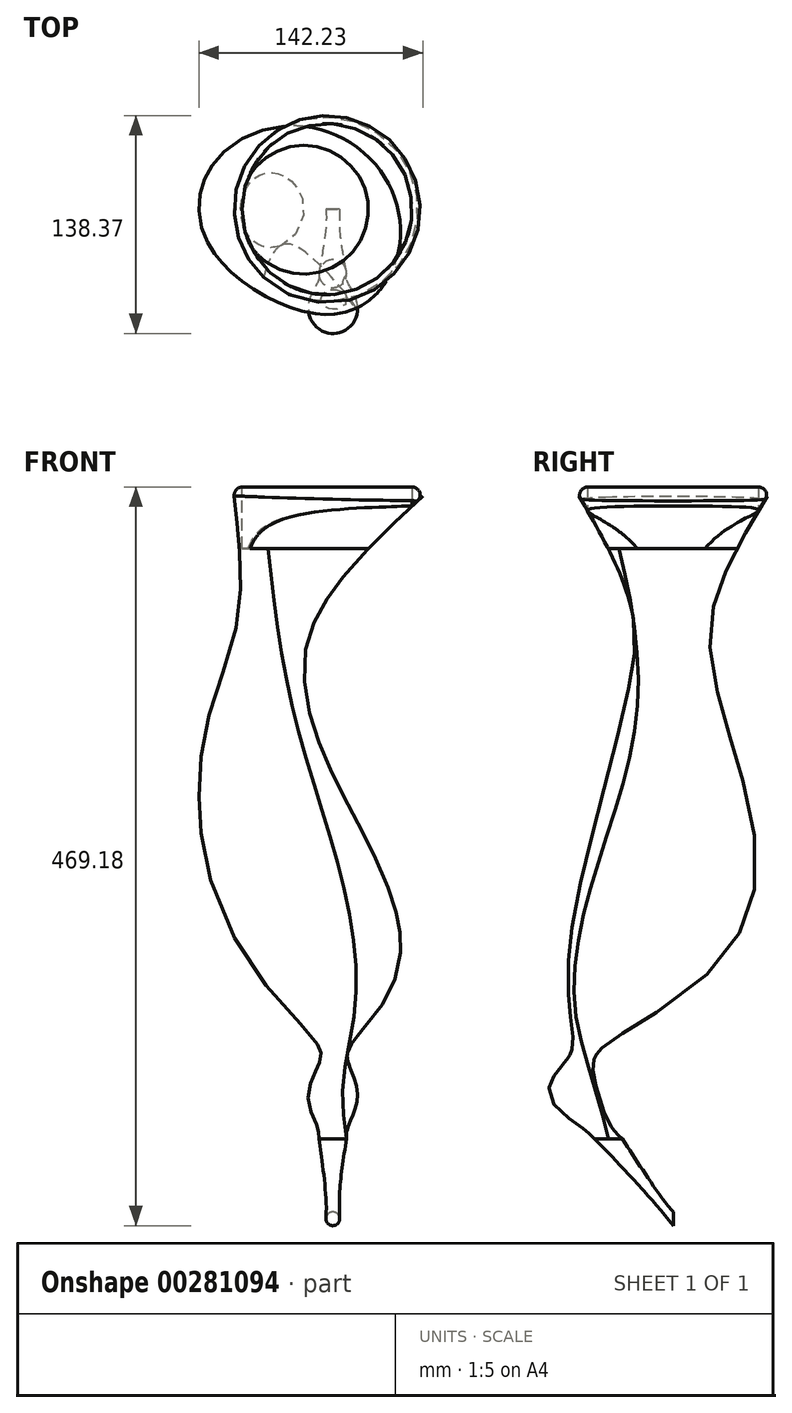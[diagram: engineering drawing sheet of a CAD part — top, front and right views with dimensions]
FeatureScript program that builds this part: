
annotation { "Feature Type Name" : "Feature", "Feature Type Description" : "" }
export const myFeature = defineFeature(function(context is Context, id is Id, definition is map)
    precondition{}
    {
        {
            var Q0;
            Q0=qCreatedBy(makeId("Front.planeOp"),FACE);
            var sketch = newSketch(context, id + "F0", { "sketchPlane" : qUnion([Q0])});
            skCircle(sketch, "E0", {"center": v(0, 0) * mm, "radius": 4.36 * mm});
            skSolve(sketch);
        }
        {
            var Q0;
            Q0=qCreatedBy(makeId("Top.planeOp"),FACE);
            cPlane(context, id + "F1", {"entities" : qUnion([Q0]), "cplaneType" : CPlaneType.OFFSET, "offset" : 50.8 * mm, "width" : 152.4 * mm, "height" : 152.4 * mm});
        }
        {
            var Q0;
            Q0=qCreatedBy(id+"F1.planeOp",FACE);
            var sketch = newSketch(context, id + "F2", { "sketchPlane" : qUnion([Q0])});
            skLineSegment(sketch, "E1", {"start": v(0, 0) * mm, "end": v(0, -41.08) * mm, "construction": true});
            skCircle(sketch, "E2", {"center": v(0, -41.08) * mm, "radius": 8.82 * mm});
            skSolve(sketch);
        }
        {
            var Q0;
            Q0=makeQuery(id+"F2.imprint","IMPRINT",FACE,{"disambiguationData":[TD([[makeQuery(id+"F2.imprint","IMPRINT",EDGE,{"derivedFrom":sQuery(id+"F2.wireOp",EDGE,"E2")}),1.0]])]});
            var Q1;
            Q1=makeQuery(id+"F0.imprint","IMPRINT",FACE,{"disambiguationData":[TD([[makeQuery(id+"F0.imprint","IMPRINT",EDGE,{"derivedFrom":sQuery(id+"F0.wireOp",EDGE,"E0")}),1.0]])]});
            loft(context, id + "F3", {"sheetProfilesArray" : [{ "sheetProfileEntities" : qUnion([Q0]) }, { "sheetProfileEntities" : qUnion([Q1]) }]});
        }
        {
            var Q0;
            Q0=qCreatedBy(id+"F1.planeOp",FACE);
            cPlane(context, id + "F4", {"entities" : qUnion([Q0]), "cplaneType" : CPlaneType.OFFSET, "offset" : 25.4 * mm, "width" : 152.4 * mm, "height" : 152.4 * mm});
        }
        {
            var Q0;
            Q0=qCreatedBy(id+"F4.planeOp",FACE);
            var sketch = newSketch(context, id + "F5", { "sketchPlane" : qUnion([Q0])});
            skLineSegment(sketch, "E3", {"start": v(0, 0) * mm, "end": v(0, -62.26) * mm, "construction": true});
            skCircle(sketch, "E4", {"center": v(0, -62.26) * mm, "radius": 15.65 * mm});
            skSolve(sketch);
        }
        {
            var Q0;
            Q0=qCreatedBy(id+"F4.planeOp",FACE);
            cPlane(context, id + "F6", {"entities" : qUnion([Q0]), "cplaneType" : CPlaneType.OFFSET, "offset" : 56.4 * mm, "width" : 152.4 * mm, "height" : 152.4 * mm});
        }
        {
            var Q0;
            Q0=qCreatedBy(id+"F6.planeOp",FACE);
            var sketch = newSketch(context, id + "F7", { "sketchPlane" : qUnion([Q0])});
            skLineSegment(sketch, "E5", {"start": v(0, 0) * mm, "end": v(0, -36.87) * mm, "construction": true});
            skCircle(sketch, "E6", {"center": v(0, -36.87) * mm, "radius": 28.94 * mm});
            skSolve(sketch);
        }
        {
            var Q0;
            Q0=qCreatedBy(id+"F6.planeOp",FACE);
            cPlane(context, id + "F8", {"entities" : qUnion([Q0]), "cplaneType" : CPlaneType.OFFSET, "offset" : 183.9 * mm, "width" : 152.4 * mm, "height" : 152.4 * mm});
        }
        {
            var Q0;
            Q0=qCreatedBy(id+"F8.planeOp",FACE);
            var sketch = newSketch(context, id + "F9", { "sketchPlane" : qUnion([Q0])});
            skLineSegment(sketch, "E7", {"start": v(0, 0) * mm, "end": v(-46.43, 0) * mm, "construction": true});
            skCircle(sketch, "E8", {"center": v(-46.43, 0) * mm, "radius": 32.98 * mm});
            skSolve(sketch);
        }
        {
            var Q0;
            Q0=qCreatedBy(id+"F8.planeOp",FACE);
            cPlane(context, id + "F10", {"entities" : qUnion([Q0]), "cplaneType" : CPlaneType.OFFSET, "offset" : 148.34 * mm, "width" : 152.4 * mm, "height" : 152.4 * mm});
        }
        {
            var Q0;
            Q0=qCreatedBy(id+"F10.planeOp",FACE);
            var sketch = newSketch(context, id + "F11", { "sketchPlane" : qUnion([Q0])});
            skCircle(sketch, "E9", {"center": v(0, 0) * mm, "radius": 63.3 * mm});
            skSolve(sketch);
        }
        {
            var Q1;
            Q1=makeQuery(id+"F3.opLoft","CAP_FACE",FACE,{"disambiguationData":[OSD([makeQuery(id+"F2.imprint","IMPRINT",FACE,{"disambiguationData":[TD([[makeQuery(id+"F2.imprint","IMPRINT",EDGE,{"derivedFrom":sQuery(id+"F2.wireOp",EDGE,"E2")}),1.0]])]})])],"isStart":true});
            var Q2;
            Q2=makeQuery(id+"F5.imprint","IMPRINT",FACE,{"disambiguationData":[TD([[makeQuery(id+"F5.imprint","IMPRINT",EDGE,{"derivedFrom":sQuery(id+"F5.wireOp",EDGE,"E4")}),1.0]])]});
            var Q3;
            Q3=makeQuery(id+"F7.imprint","IMPRINT",FACE,{"disambiguationData":[TD([[makeQuery(id+"F7.imprint","IMPRINT",EDGE,{"derivedFrom":sQuery(id+"F7.wireOp",EDGE,"E6")}),1.0]])]});
            var Q4;
            Q4=makeQuery(id+"F9.imprint","IMPRINT",FACE,{"disambiguationData":[TD([[makeQuery(id+"F9.imprint","IMPRINT",EDGE,{"derivedFrom":sQuery(id+"F9.wireOp",EDGE,"E8")}),1.0]])]});
            var Q5;
            Q5=makeQuery(id+"F11.imprint","IMPRINT",FACE,{"disambiguationData":[TD([[makeQuery(id+"F11.imprint","IMPRINT",EDGE,{"derivedFrom":sQuery(id+"F11.wireOp",EDGE,"E9")}),1.0]])]});
            loft(context, id + "F12", {"operationType" : NewBodyOperationType.ADD, "sheetProfilesArray" : [{ "sheetProfileEntities" : qUnion([Q1]) }, { "sheetProfileEntities" : qUnion([Q2]) }, { "sheetProfileEntities" : qUnion([Q3]) }, { "sheetProfileEntities" : qUnion([Q4]) }, { "sheetProfileEntities" : qUnion([Q5]) }]});
        }
        {
            var Q0;
            Q0=makeQuery(id+"F12.opLoft","MID_CAP_EDGE",EDGE,{"disambiguationData":[OSD([sQuery(id+"F2.wireOp",EDGE,"E2"),sQuery(id+"F11.wireOp",EDGE,"E9")])],"capPos":4.0});
            fillet(context, id + "F13", {"entities" : qUnion([Q0]), "radius" : 5.08 * mm, "tangentPropagation" : true, "allowEdgeOverflow" : false});
        }
        {
            var Q0;
            Q0=makeQuery(id+"F12.opLoft","CAP_FACE",FACE,{"disambiguationData":[OSD([makeQuery(id+"F11.imprint","IMPRINT",FACE,{"disambiguationData":[TD([[makeQuery(id+"F11.imprint","IMPRINT",EDGE,{"derivedFrom":sQuery(id+"F11.wireOp",EDGE,"E9")}),1.0]])]})])],"isStart":true});
            extrude(context, id + "F14", {"entities" : qUnion([Q0]), "operationType" : NewBodyOperationType.REMOVE, "oppositeDirection" : true, "depth" : 39.12 * mm});
        }
    });
